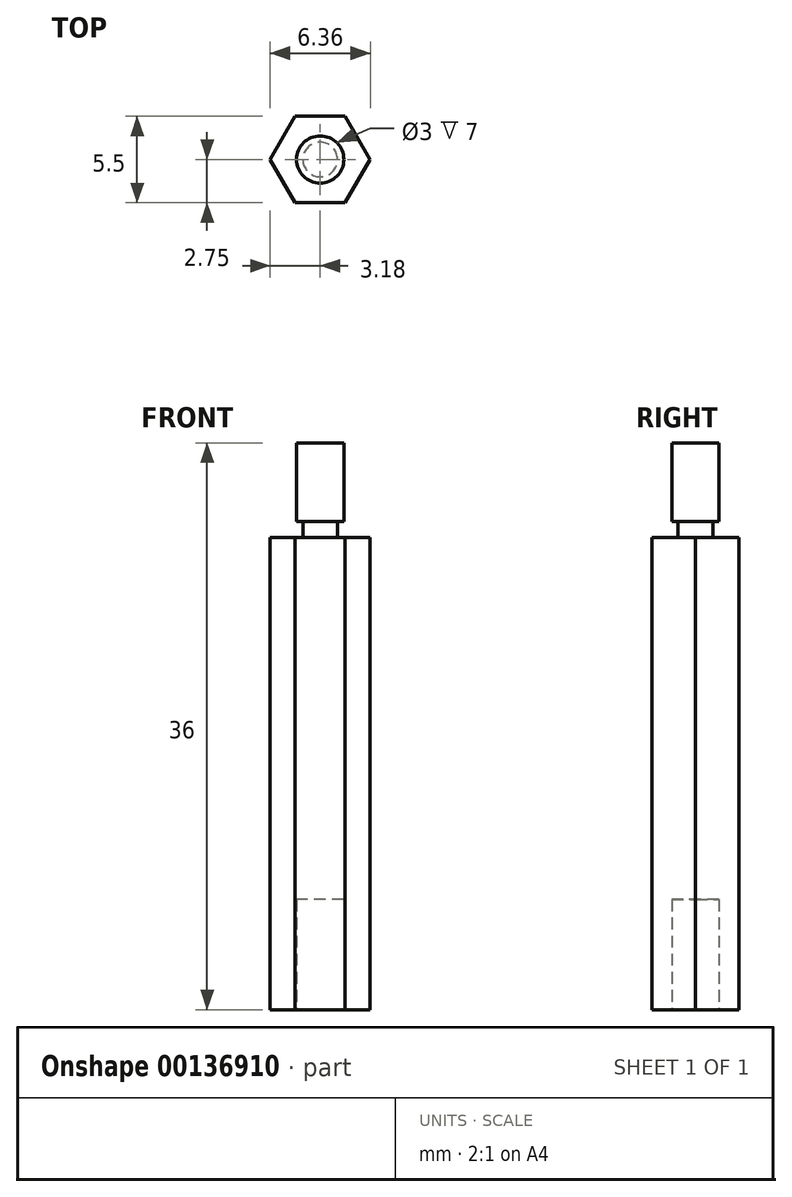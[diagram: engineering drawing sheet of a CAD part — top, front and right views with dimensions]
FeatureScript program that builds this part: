
annotation { "Feature Type Name" : "Feature", "Feature Type Description" : "" }
export const myFeature = defineFeature(function(context is Context, id is Id, definition is map)
    precondition{}
    {
        {
            var Q0;
            Q0=qCreatedBy(makeId("Top.planeOp"),FACE);
            var sketch = newSketch(context, id + "F0", { "sketchPlane" : qUnion([Q0])});
            skCircle(sketch, "E0.cCircle", {"center": v(0, 0) * mm, "radius": 2.75 * mm, "construction": true});
            skLineSegment(sketch, "E0.0", {"start": v(-1.59, 2.75) * mm, "end": v(1.59, 2.75) * mm});
            skLineSegment(sketch, "E0.1", {"start": v(1.59, 2.75) * mm, "end": v(3.18, 0) * mm});
            skLineSegment(sketch, "E0.2", {"start": v(3.18, 0) * mm, "end": v(1.59, -2.75) * mm});
            skLineSegment(sketch, "E0.3", {"start": v(1.59, -2.75) * mm, "end": v(-1.59, -2.75) * mm});
            skLineSegment(sketch, "E0.4", {"start": v(-1.59, -2.75) * mm, "end": v(-3.18, 0) * mm});
            skLineSegment(sketch, "E0.5", {"start": v(-3.18, 0) * mm, "end": v(-1.59, 2.75) * mm});
            skPoint(sketch, "E0.0.midPoint", {"position": v(0, 2.75) * mm});
            skSolve(sketch);
        }
        {
            var Q0;
            Q0=makeQuery(id+"F0.imprint","IMPRINT",FACE,{"disambiguationData":[TD([[makeQuery(id+"F0.imprint","IMPRINT",EDGE,{"derivedFrom":sQuery(id+"F0.wireOp",EDGE,"E0.0")}),-1.0]])]});
            extrude(context, id + "F1", {"entities" : qUnion([Q0]), "depth" : 30 * mm});
        }
        {
            var Q0;
            Q0=makeQuery(id+"F1.opExtrude","CAP_FACE",FACE,{"disambiguationData":[OSD([sQuery(id+"F0.wireOp",EDGE,"E0.0"),sQuery(id+"F0.wireOp",EDGE,"E0.1"),sQuery(id+"F0.wireOp",EDGE,"E0.2"),sQuery(id+"F0.wireOp",EDGE,"E0.3"),sQuery(id+"F0.wireOp",EDGE,"E0.4"),sQuery(id+"F0.wireOp",EDGE,"E0.5")])],"isStart":false});
            var sketch = newSketch(context, id + "F2", { "sketchPlane" : qUnion([Q0])});
            skCircle(sketch, "E1", {"center": v(0, 0) * mm, "radius": 1.1 * mm});
            skSolve(sketch);
        }
        {
            var Q0;
            Q0=makeQuery(id+"F2.imprint","IMPRINT",FACE,{"disambiguationData":[TD([[makeQuery(id+"F2.imprint","IMPRINT",EDGE,{"derivedFrom":sQuery(id+"F2.wireOp",EDGE,"E1")}),1.0]])]});
            extrude(context, id + "F3", {"entities" : qUnion([Q0]), "operationType" : NewBodyOperationType.ADD, "depth" : 1 * mm});
        }
        {
            var Q0;
            Q0=makeQuery(id+"F3.opExtrude","CAP_FACE",FACE,{"disambiguationData":[OSD([sQuery(id+"F2.wireOp",EDGE,"E1")])],"isStart":false});
            var sketch = newSketch(context, id + "F4", { "sketchPlane" : qUnion([Q0])});
            skCircle(sketch, "E2", {"center": v(0, 0) * mm, "radius": 1.5 * mm});
            skSolve(sketch);
        }
        {
            var Q0;
            Q0 = qSketchRegion(id + "F4", true);
            extrude(context, id + "F5", {"entities" : qUnion([Q0]), "operationType" : NewBodyOperationType.ADD, "depth" : 5 * mm});
        }
        {
            var Q0;
            Q0=qCreatedBy(makeId("Top.planeOp"),FACE);
            var sketch = newSketch(context, id + "F6", { "sketchPlane" : qUnion([Q0])});
            skCircle(sketch, "E3", {"center": v(0, 0) * mm, "radius": 1.5 * mm});
            skSolve(sketch);
        }
        {
            var Q0;
            Q0=makeQuery(id+"F6.imprint","IMPRINT",FACE,{"disambiguationData":[TD([[makeQuery(id+"F6.imprint","IMPRINT",EDGE,{"derivedFrom":sQuery(id+"F6.wireOp",EDGE,"E3")}),1.0]])]});
            var Q1;
            Q1=sQuery(id+"F6.wireOp",EDGE,"E3");
            extrude(context, id + "F7", {"entities" : qUnion([Q0]), "operationType" : NewBodyOperationType.REMOVE, "surfaceEntities" : qUnion([Q1]), "depth" : 7 * mm});
        }
    });
